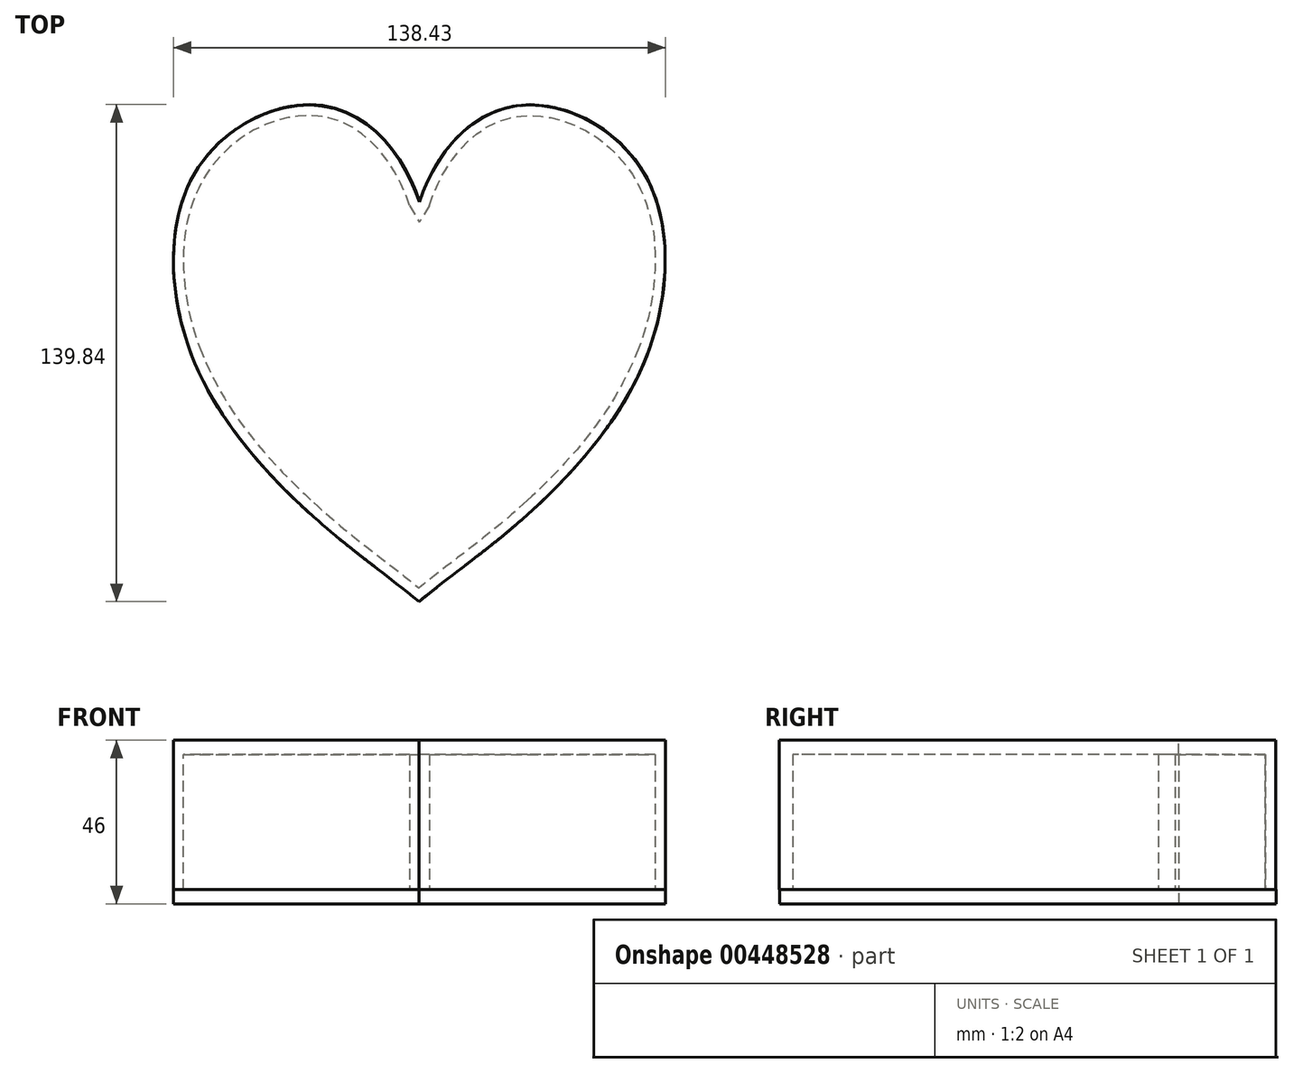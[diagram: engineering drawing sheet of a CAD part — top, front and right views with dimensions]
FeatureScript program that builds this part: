
annotation { "Feature Type Name" : "Feature", "Feature Type Description" : "" }
export const myFeature = defineFeature(function(context is Context, id is Id, definition is map)
    precondition{}
    {
        {
            var Q0;
            Q0=qCreatedBy(makeId("Top.planeOp"),FACE);
            var sketch = newSketch(context, id + "F0", { "sketchPlane" : qUnion([Q0])});
            skFitSpline(sketch, "E0", {"points": [v(3.87, 9.7) * mm, v(-7.82, 29.67) * mm, v(-30.39, 37.98) * mm, v(-60.25, 17.9) * mm, v(-58.9, -36.27) * mm, v(-23.65, -80.02) * mm, v(3.87, -101.98) * mm], "startDerivative": vector(-43.82, 145.7) * mm, "endDerivative": vector(235.36, -190.2) * mm});
            skFitSpline(sketch, "E1.MirrorCS", {"points": [v(3.16, 9.7) * mm, v(14.85, 29.67) * mm, v(37.42, 37.98) * mm, v(67.28, 17.9) * mm, v(65.92, -36.27) * mm, v(30.68, -80.02) * mm, v(3.16, -101.83) * mm], "startDerivative": vector(43.82, 145.7) * mm, "endDerivative": vector(-235.36, -190.2) * mm});
            skFitSpline(sketch, "E2", {"points": [v(3.87, 9.7) * mm, v(-7.82, 29.67) * mm, v(-30.39, 37.98) * mm, v(-60.25, 17.9) * mm, v(-58.9, -36.27) * mm, v(-23.65, -80.02) * mm, v(3.87, -101.98) * mm], "startDerivative": vector(-43.82, 145.7) * mm, "endDerivative": vector(235.36, -190.2) * mm});
            skFitSpline(sketch, "E3", {"points": [v(3.87, 9.7) * mm, v(-7.82, 29.67) * mm, v(-30.39, 37.98) * mm, v(-60.25, 17.9) * mm, v(-58.9, -36.27) * mm, v(-23.65, -80.02) * mm, v(3.87, -101.98) * mm], "startDerivative": vector(-43.82, 145.7) * mm, "endDerivative": vector(235.36, -190.2) * mm});
            skLineSegment(sketch, "E4", {"start": v(-58.17, -30.08) * mm, "end": v(-61.62, -29.33) * mm});
            skSolve(sketch);
        }
        {
            var Q0;
            Q0=qCreatedBy(makeId("Top.planeOp"),FACE);
            var sketch = newSketch(context, id + "F1", { "sketchPlane" : qUnion([Q0])});
            skFitSpline(sketch, "E5", {"points": [v(3.81, 9.58) * mm, v(-7.88, 29.55) * mm, v(-30.45, 37.86) * mm, v(-60.31, 17.79) * mm, v(-58.95, -36.39) * mm, v(-23.71, -80.14) * mm, v(3.81, -102.1) * mm], "startDerivative": vector(-43.82, 145.7) * mm, "endDerivative": vector(235.36, -190.2) * mm});
            skFitSpline(sketch, "E6.MirrorCS", {"points": [v(3.1, 9.58) * mm, v(14.8, 29.55) * mm, v(37.36, 37.86) * mm, v(67.22, 17.79) * mm, v(65.86, -36.39) * mm, v(30.62, -80.14) * mm, v(3.1, -101.95) * mm], "startDerivative": vector(43.82, 145.7) * mm, "endDerivative": vector(-235.36, -190.2) * mm});
            skLineSegment(sketch, "E7", {"start": v(3.81, -101.37) * mm, "end": v(3.81, -52.12) * mm, "construction": true});
            skLineSegment(sketch, "E8", {"start": v(3.81, -52.12) * mm, "end": v(3.81, -44.12) * mm, "construction": true});
            skLineSegment(sketch, "E9", {"start": v(-10.3, -40.95) * mm, "end": v(-58.23, -30.2) * mm, "construction": true});
            skLineSegment(sketch, "E10", {"start": v(-58.23, -30.2) * mm, "end": v(-10.3, -40.95) * mm});
            skLineSegment(sketch, "E11", {"start": v(3.81, -44.12) * mm, "end": v(13.66, -0.2) * mm, "construction": true});
            skLineSegment(sketch, "E12", {"start": v(-62.29, 1.41) * mm, "end": v(-3.74, -11.72) * mm, "construction": true});
            skLineSegment(sketch, "E13", {"start": v(-3.74, -11.72) * mm, "end": v(-0.46, 2.97) * mm});
            skLineSegment(sketch, "E14", {"start": v(-0.46, 2.97) * mm, "end": v(-3.74, -11.72) * mm});
            skLineSegment(sketch, "E15", {"start": v(-3.74, -11.72) * mm, "end": v(-10.3, -40.95) * mm});
            skLineSegment(sketch, "E16.MirrorCS", {"start": v(65.08, -30.38) * mm, "end": v(17.93, -40.95) * mm});
            skLineSegment(sketch, "E17.MirrorCS", {"start": v(69.92, 1.41) * mm, "end": v(11.37, -11.72) * mm, "construction": true});
            skLineSegment(sketch, "E18.MirrorCS", {"start": v(11.37, -11.72) * mm, "end": v(17.93, -40.95) * mm});
            skLineSegment(sketch, "E19.MirrorCS", {"start": v(8.09, 2.97) * mm, "end": v(11.37, -11.72) * mm});
            skLineSegment(sketch, "E20.trimOffspring", {"start": v(8.09, 2.97) * mm, "end": v(64.93, 15.7) * mm});
            skPoint(sketch, "E21.MirrorCS.start.orphan", {"position": v(-6.03, -0.2) * mm});
            skLineSegment(sketch, "E22.trimOffspring", {"start": v(-0.46, 2.97) * mm, "end": v(-57.95, 15.85) * mm});
            skPoint(sketch, "E23.orphan", {"position": v(3.81, -44.12) * mm});
            skFitSpline(sketch, "E24", {"points": [v(3.81, 9.58) * mm, v(-7.88, 29.55) * mm, v(-30.45, 37.86) * mm, v(-60.31, 17.79) * mm, v(-58.95, -36.39) * mm, v(-23.71, -80.14) * mm, v(3.81, -102.1) * mm], "startDerivative": vector(-43.82, 145.7) * mm, "endDerivative": vector(235.36, -190.2) * mm});
            skLineSegment(sketch, "E25", {"start": v(-57.95, 15.85) * mm, "end": v(-59.4, 9.34) * mm, "construction": true});
            skLineSegment(sketch, "E26", {"start": v(-58.23, -30.2) * mm, "end": v(-55, -15.82) * mm, "construction": true});
            skLineSegment(sketch, "E27", {"start": v(3.81, -52.12) * mm, "end": v(-26.19, -52.12) * mm});
            skLineSegment(sketch, "E28", {"start": v(-26.19, -52.12) * mm, "end": v(-26.19, -73.92) * mm});
            skFitSpline(sketch, "E29", {"points": [v(3.81, 9.58) * mm, v(-7.88, 29.55) * mm, v(-30.45, 37.86) * mm, v(-60.31, 17.79) * mm, v(-58.95, -36.39) * mm, v(-23.71, -80.14) * mm, v(3.81, -102.1) * mm], "startDerivative": vector(-43.82, 145.7) * mm, "endDerivative": vector(235.36, -190.2) * mm, "construction": true});
            skFitSpline(sketch, "E30.0", {"points": [v(0.94, 8.71) * mm, v(0.52, 10.13) * mm, v(-0.56, 13.15) * mm, v(-2.82, 17.89) * mm, v(-5.68, 22.52) * mm, v(-8.52, 26.01) * mm, v(-11.03, 28.44) * mm, v(-13.71, 30.6) * mm, v(-17.35, 32.79) * mm, v(-21.33, 34.2) * mm, v(-24.7, 34.83) * mm, v(-27.34, 35.02) * mm, v(-30.07, 34.93) * mm, v(-32.9, 34.53) * mm, v(-35.82, 33.82) * mm, v(-39.76, 32.48) * mm, v(-44.64, 30.06) * mm, v(-49.2, 26.71) * mm, v(-52.5, 23.53) * mm, v(-54.75, 20.9) * mm, v(-56.75, 18.04) * mm, v(-58.47, 14.96) * mm, v(-59.9, 11.63) * mm, v(-61.42, 6.9) * mm, v(-62.6, 0.5) * mm, v(-62.89, -7.72) * mm, v(-62.06, -16.26) * mm, v(-60.14, -24.88) * mm, v(-57.68, -31.94) * mm, v(-55.22, -37.4) * mm, v(-52.43, -42.72) * mm, v(-48.43, -49.11) * mm, v(-43.04, -56.3) * mm, v(-37.32, -62.93) * mm, v(-32.48, -67.94) * mm, v(-28.68, -71.61) * mm, v(-25.91, -74.18) * mm, v(-23.25, -76.57) * mm, v(-20.72, -78.77) * mm, v(-18.34, -80.78) * mm, v(-15.27, -83.3) * mm, v(-11.52, -86.26) * mm, v(-6.7, -89.98) * mm, v(-1.19, -94.27) * mm, v(3.24, -97.78) * mm, v(5.7, -99.77) * mm], "construction": true});
            skFitSpline(sketch, "E30.1", {"points": [v(0.94, 8.71) * mm, v(0.52, 10.13) * mm, v(-0.56, 13.15) * mm, v(-2.82, 17.89) * mm, v(-5.68, 22.52) * mm, v(-8.52, 26.01) * mm, v(-11.03, 28.44) * mm, v(-13.71, 30.6) * mm, v(-17.35, 32.79) * mm, v(-21.33, 34.2) * mm, v(-24.7, 34.83) * mm, v(-27.34, 35.02) * mm, v(-30.07, 34.93) * mm, v(-32.9, 34.53) * mm, v(-35.82, 33.82) * mm, v(-39.76, 32.48) * mm, v(-44.64, 30.06) * mm, v(-49.2, 26.71) * mm, v(-52.5, 23.53) * mm, v(-54.75, 20.9) * mm, v(-56.75, 18.04) * mm, v(-58.47, 14.96) * mm, v(-59.9, 11.63) * mm, v(-61.42, 6.9) * mm, v(-62.6, 0.5) * mm, v(-62.89, -7.72) * mm, v(-62.06, -16.26) * mm, v(-60.14, -24.88) * mm, v(-57.68, -31.94) * mm, v(-55.22, -37.4) * mm, v(-52.43, -42.72) * mm, v(-48.43, -49.11) * mm, v(-43.04, -56.3) * mm, v(-37.32, -62.93) * mm, v(-32.48, -67.94) * mm, v(-28.68, -71.61) * mm, v(-25.91, -74.18) * mm, v(-23.25, -76.57) * mm, v(-20.72, -78.77) * mm, v(-18.34, -80.78) * mm, v(-15.27, -83.3) * mm, v(-11.52, -86.26) * mm, v(-6.7, -89.98) * mm, v(-1.19, -94.27) * mm, v(3.24, -97.78) * mm, v(5.7, -99.77) * mm]});
            skLineSegment(sketch, "E31", {"start": v(-26.19, -73.92) * mm, "end": v(-24.2, -75.71) * mm, "construction": true});
            skFitSpline(sketch, "E32", {"points": [v(3.81, 9.58) * mm, v(-7.88, 29.55) * mm, v(-30.45, 37.86) * mm, v(-60.31, 17.79) * mm, v(-58.95, -36.39) * mm, v(-23.71, -80.14) * mm, v(3.81, -102.1) * mm], "startDerivative": vector(-43.82, 145.7) * mm, "endDerivative": vector(235.36, -190.2) * mm});
            skFitSpline(sketch, "E33", {"points": [v(3.81, 9.58) * mm, v(-7.88, 29.55) * mm, v(-30.45, 37.86) * mm, v(-60.31, 17.79) * mm, v(-58.95, -36.39) * mm, v(-23.71, -80.14) * mm, v(3.81, -102.1) * mm], "startDerivative": vector(-43.82, 145.7) * mm, "endDerivative": vector(235.36, -190.2) * mm, "construction": true});
            skFitSpline(sketch, "E34.0", {"points": [v(0.94, 8.71) * mm, v(0.52, 10.13) * mm, v(-0.56, 13.15) * mm, v(-2.82, 17.89) * mm, v(-5.68, 22.52) * mm, v(-8.52, 26.01) * mm, v(-11.03, 28.44) * mm, v(-13.71, 30.6) * mm, v(-17.35, 32.79) * mm, v(-21.33, 34.2) * mm, v(-24.7, 34.83) * mm, v(-27.34, 35.02) * mm, v(-30.07, 34.93) * mm, v(-32.9, 34.53) * mm, v(-35.82, 33.82) * mm, v(-39.76, 32.48) * mm, v(-44.64, 30.06) * mm, v(-49.2, 26.71) * mm, v(-52.5, 23.53) * mm, v(-54.75, 20.9) * mm, v(-56.75, 18.04) * mm, v(-58.47, 14.96) * mm, v(-59.9, 11.63) * mm, v(-61.42, 6.9) * mm, v(-62.6, 0.5) * mm, v(-62.89, -7.72) * mm, v(-62.06, -16.26) * mm, v(-60.14, -24.88) * mm, v(-57.68, -31.94) * mm, v(-55.22, -37.4) * mm, v(-52.43, -42.72) * mm, v(-48.43, -49.11) * mm, v(-43.04, -56.3) * mm, v(-37.32, -62.93) * mm, v(-32.48, -67.94) * mm, v(-28.68, -71.61) * mm, v(-25.91, -74.18) * mm, v(-23.25, -76.57) * mm, v(-20.72, -78.77) * mm, v(-18.34, -80.78) * mm, v(-15.27, -83.3) * mm, v(-11.52, -86.26) * mm, v(-6.7, -89.98) * mm, v(-1.19, -94.27) * mm, v(3.24, -97.78) * mm, v(5.7, -99.77) * mm]});
            skFitSpline(sketch, "E35.0", {"points": [v(0.94, 8.71) * mm, v(0.52, 10.13) * mm, v(-0.56, 13.15) * mm, v(-2.82, 17.89) * mm, v(-5.68, 22.52) * mm, v(-8.52, 26.01) * mm, v(-11.03, 28.44) * mm, v(-13.71, 30.6) * mm, v(-17.35, 32.79) * mm, v(-21.33, 34.2) * mm, v(-24.7, 34.83) * mm, v(-27.34, 35.02) * mm, v(-30.07, 34.93) * mm, v(-32.9, 34.53) * mm, v(-35.82, 33.82) * mm, v(-39.76, 32.48) * mm, v(-44.64, 30.06) * mm, v(-49.2, 26.71) * mm, v(-52.5, 23.53) * mm, v(-54.75, 20.9) * mm, v(-56.75, 18.04) * mm, v(-58.47, 14.96) * mm, v(-59.9, 11.63) * mm, v(-61.42, 6.9) * mm, v(-62.6, 0.5) * mm, v(-62.89, -7.72) * mm, v(-62.06, -16.26) * mm, v(-60.14, -24.88) * mm, v(-57.68, -31.94) * mm, v(-55.22, -37.4) * mm, v(-52.43, -42.72) * mm, v(-48.43, -49.11) * mm, v(-43.04, -56.3) * mm, v(-37.32, -62.93) * mm, v(-32.48, -67.94) * mm, v(-28.68, -71.61) * mm, v(-25.91, -74.18) * mm, v(-23.25, -76.57) * mm, v(-20.72, -78.77) * mm, v(-18.34, -80.78) * mm, v(-15.27, -83.3) * mm, v(-11.52, -86.26) * mm, v(-6.7, -89.98) * mm, v(-1.19, -94.27) * mm, v(3.24, -97.78) * mm, v(5.7, -99.77) * mm]});
            skLineSegment(sketch, "E36", {"start": v(-26.19, -73.92) * mm, "end": v(-26.2, -77.95) * mm});
            skLineSegment(sketch, "E37", {"start": v(-58.23, -30.2) * mm, "end": v(-61.68, -29.45) * mm});
            skLineSegment(sketch, "E38", {"start": v(-57.95, 15.85) * mm, "end": v(-60.97, 16.54) * mm});
            skLineSegment(sketch, "E39.MirrorCS", {"start": v(3.81, -52.12) * mm, "end": v(33.81, -52.12) * mm});
            skLineSegment(sketch, "E40.MirrorCS", {"start": v(33.81, -52.12) * mm, "end": v(33.81, -73.28) * mm});
            skFitSpline(sketch, "E41", {"points": [v(3.1, 9.58) * mm, v(14.8, 29.55) * mm, v(37.36, 37.86) * mm, v(67.22, 17.79) * mm, v(65.86, -36.39) * mm, v(30.62, -80.14) * mm, v(3.1, -101.95) * mm], "startDerivative": vector(43.82, 145.7) * mm, "endDerivative": vector(-235.36, -190.2) * mm, "construction": true});
            skFitSpline(sketch, "E42.0", {"points": [v(5.97, 8.71) * mm, v(6.4, 10.13) * mm, v(7.47, 13.15) * mm, v(9.73, 17.89) * mm, v(12.59, 22.52) * mm, v(15.43, 26) * mm, v(17.94, 28.43) * mm, v(20.62, 30.6) * mm, v(24.26, 32.79) * mm, v(28.24, 34.2) * mm, v(31.61, 34.82) * mm, v(34.24, 35.02) * mm, v(36.97, 34.93) * mm, v(39.8, 34.53) * mm, v(42.72, 33.83) * mm, v(46.65, 32.48) * mm, v(51.54, 30.06) * mm, v(56.1, 26.72) * mm, v(59.4, 23.55) * mm, v(61.65, 20.92) * mm, v(63.66, 18.06) * mm, v(65.37, 14.98) * mm, v(66.8, 11.66) * mm, v(68.32, 6.93) * mm, v(69.5, 0.54) * mm, v(69.8, -7.68) * mm, v(68.97, -16.22) * mm, v(67.06, -24.84) * mm, v(64.6, -31.9) * mm, v(62.15, -37.36) * mm, v(59.37, -42.69) * mm, v(55.37, -49.09) * mm, v(49.99, -56.28) * mm, v(44.27, -62.92) * mm, v(39.43, -67.93) * mm, v(35.63, -71.6) * mm, v(32.86, -74.17) * mm, v(30.2, -76.55) * mm, v(27.67, -78.73) * mm, v(25.28, -80.73) * mm, v(22.22, -83.22) * mm, v(18.46, -86.16) * mm, v(13.64, -89.85) * mm, v(8.1, -94.12) * mm, v(3.68, -97.63) * mm, v(1.21, -99.62) * mm]});
            skLineSegment(sketch, "E43", {"start": v(64.93, 15.7) * mm, "end": v(67.95, 16.4) * mm});
            skLineSegment(sketch, "E44", {"start": v(3.46, 10.71) * mm, "end": v(3.46, 4.97) * mm});
            skLineSegment(sketch, "E45", {"start": v(0.6, 9.78) * mm, "end": v(3.46, 4.97) * mm});
            skLineSegment(sketch, "E46", {"start": v(6.3, 9.78) * mm, "end": v(3.46, 4.97) * mm});
            skFitSpline(sketch, "E47.trimOffspring", {"points": [v(5.97, 8.71) * mm, v(6.4, 10.13) * mm, v(7.47, 13.15) * mm, v(9.73, 17.89) * mm, v(12.59, 22.52) * mm, v(15.43, 26) * mm, v(17.94, 28.43) * mm, v(20.62, 30.6) * mm, v(24.26, 32.79) * mm, v(28.24, 34.2) * mm, v(31.61, 34.82) * mm, v(34.24, 35.02) * mm, v(36.97, 34.93) * mm, v(39.8, 34.53) * mm, v(42.72, 33.83) * mm, v(46.65, 32.48) * mm, v(51.54, 30.06) * mm, v(56.1, 26.72) * mm, v(59.4, 23.55) * mm, v(61.65, 20.92) * mm, v(63.66, 18.06) * mm, v(65.37, 14.98) * mm, v(66.8, 11.66) * mm, v(68.32, 6.93) * mm, v(69.5, 0.54) * mm, v(69.8, -7.68) * mm, v(68.97, -16.22) * mm, v(67.06, -24.84) * mm, v(64.6, -31.9) * mm, v(62.15, -37.36) * mm, v(59.37, -42.69) * mm, v(55.37, -49.09) * mm, v(49.99, -56.28) * mm, v(44.27, -62.92) * mm, v(39.43, -67.93) * mm, v(35.63, -71.6) * mm, v(32.86, -74.17) * mm, v(30.2, -76.55) * mm, v(27.67, -78.73) * mm, v(25.28, -80.73) * mm, v(22.22, -83.22) * mm, v(18.46, -86.16) * mm, v(13.64, -89.85) * mm, v(8.1, -94.12) * mm, v(3.68, -97.63) * mm, v(1.21, -99.62) * mm]});
            skLineSegment(sketch, "E48", {"start": v(33.81, -73.28) * mm, "end": v(33.86, -77.3) * mm});
            skLineSegment(sketch, "E49", {"start": v(65.08, -30.38) * mm, "end": v(68.52, -29.65) * mm});
            skSolve(sketch);
        }
        {
            var Q0;
            Q0=makeQuery(id+"F0.imprint","IMPRINT",FACE,{"disambiguationData":[TD([[makeQuery(id+"F0.imprint","IMPRINT",EDGE,{"derivedFrom":sQuery(id+"F0.wireOp",EDGE,"E0")}),1.0]])]});
            extrude(context, id + "F2", {"entities" : qUnion([Q0]), "oppositeDirection" : true, "depth" : 4 * mm});
        }
        {
            var Q0;
            Q0 = qSketchRegion(id + "F1", true);
            extrude(context, id + "F3", {"entities" : qUnion([Q0]), "operationType" : NewBodyOperationType.ADD, "depth" : 38 * mm});
        }
        {
            var Q0;
            Q0=makeQuery(id+"F3.opExtrude","CAP_FACE",FACE,{"disambiguationData":[OSD([sQuery(id+"F1.wireOp",EDGE,"E5"),sQuery(id+"F1.wireOp",EDGE,"E6.MirrorCS"),sQuery(id+"F1.wireOp",EDGE,"E10"),sQuery(id+"F1.wireOp",EDGE,"E14"),sQuery(id+"F1.wireOp",EDGE,"E15"),sQuery(id+"F1.wireOp",EDGE,"E16.MirrorCS"),sQuery(id+"F1.wireOp",EDGE,"E18.MirrorCS"),sQuery(id+"F1.wireOp",EDGE,"E19.MirrorCS"),sQuery(id+"F1.wireOp",EDGE,"E20.trimOffspring"),sQuery(id+"F1.wireOp",EDGE,"E22.trimOffspring"),sQuery(id+"F1.wireOp",EDGE,"E24"),sQuery(id+"F1.wireOp",EDGE,"E27"),sQuery(id+"F1.wireOp",EDGE,"E28"),sQuery(id+"F1.wireOp",EDGE,"E32"),sQuery(id+"F1.wireOp",EDGE,"E36"),sQuery(id+"F1.wireOp",EDGE,"E37"),sQuery(id+"F1.wireOp",EDGE,"E38"),sQuery(id+"F1.wireOp",EDGE,"E39.MirrorCS"),sQuery(id+"F1.wireOp",EDGE,"E40.MirrorCS"),sQuery(id+"F1.wireOp",EDGE,"E6.MirrorCS"),sQuery(id+"F1.wireOp",EDGE,"E43"),sQuery(id+"F1.wireOp",EDGE,"E48"),sQuery(id+"F1.wireOp",EDGE,"E49")])],"isStart":false});
            var sketch = newSketch(context, id + "F4", { "sketchPlane" : qUnion([Q0])});
            skFitSpline(sketch, "E50", {"points": [v(3.81, 9.58) * mm, v(-7.88, 29.55) * mm, v(-30.45, 37.86) * mm, v(-60.31, 17.79) * mm, v(-58.95, -36.39) * mm, v(-23.71, -80.14) * mm, v(3.81, -102.1) * mm], "startDerivative": vector(-43.82, 145.7) * mm, "endDerivative": vector(235.36, -190.2) * mm});
            skFitSpline(sketch, "E51.MirrorCS", {"points": [v(3.1, 9.58) * mm, v(14.8, 29.55) * mm, v(37.36, 37.86) * mm, v(67.22, 17.79) * mm, v(65.86, -36.39) * mm, v(30.62, -80.14) * mm, v(3.1, -101.95) * mm], "startDerivative": vector(43.82, 145.7) * mm, "endDerivative": vector(-235.36, -190.2) * mm});
            skFitSpline(sketch, "E52", {"points": [v(3.81, 9.58) * mm, v(-7.88, 29.55) * mm, v(-30.45, 37.86) * mm, v(-60.31, 17.79) * mm, v(-58.95, -36.39) * mm, v(-23.71, -80.14) * mm, v(3.81, -102.1) * mm], "startDerivative": vector(-43.82, 145.7) * mm, "endDerivative": vector(235.36, -190.2) * mm});
            skFitSpline(sketch, "E53", {"points": [v(3.81, 9.58) * mm, v(-7.88, 29.55) * mm, v(-30.45, 37.86) * mm, v(-60.31, 17.79) * mm, v(-58.95, -36.39) * mm, v(-23.71, -80.14) * mm, v(3.81, -102.1) * mm], "startDerivative": vector(-43.82, 145.7) * mm, "endDerivative": vector(235.36, -190.2) * mm});
            skFitSpline(sketch, "E54", {"points": [v(3.81, 9.58) * mm, v(-7.88, 29.55) * mm, v(-30.45, 37.86) * mm, v(-60.31, 17.79) * mm, v(-58.95, -36.39) * mm, v(-23.71, -80.14) * mm, v(3.81, -102.1) * mm], "startDerivative": vector(-43.82, 145.7) * mm, "endDerivative": vector(235.36, -190.2) * mm});
            skLineSegment(sketch, "E55", {"start": v(-58.23, -30.2) * mm, "end": v(-61.68, -29.45) * mm});
            skSolve(sketch);
        }
        {
            var Q0;
            Q0=qSketchRegion(id+"F4",true);
            extrude(context, id + "F5", {"entities" : qUnion([Q0]), "operationType" : NewBodyOperationType.ADD, "depth" : 4 * mm});
        }
    });
